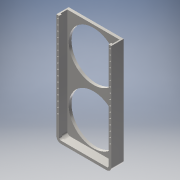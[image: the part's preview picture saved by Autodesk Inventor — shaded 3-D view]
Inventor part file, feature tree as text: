
AUTODESK INVENTOR PART (.ipt)
format: ipt  version: 2016 (Build 200138000, 138)  size: 247,296 bytes
history: native  units: mm
features: sketch x6, projected_geometry x6, extrude x4, hole x2
ambient origin geometry x8: Origin, YZ Plane, XZ Plane, XY Plane, X Axis, Y Axis, Z Axis, Center Point
bodies: Solid1 (feature_tree)
feature tree (18):
  extrude  "Extrusion1"  Depth=240.0mm
  extrude  "Extrusion2"  Depth=6.0mm
  extrude  "Extrusion3"  Depth=6.0mm
  extrude  "Extrusion4"  Depth=3.0mm
  hole  "Hole1"  [1 undecoded]
  hole  "Hole2"  [1 undecoded]
  sketch  "Sketch1"  dims[d0=120.0mm d1=240.0mm]
  sketch  "Sketch2"  dims[d2=120.0mm d3=6.0mm]
  projected_geometry  "Projected Loop1"
  sketch  "Sketch3"  dims[d4=10.0mm d5=6.0mm]
  projected_geometry  "Projected Loop2"
  sketch  "Sketch5"  dims[d6=0.0mm d7=3.0mm]
  projected_geometry  "Projected Loop3"
  sketch  "Sketch6"  dims[d8=15.0mm d9=0.0mm]
  projected_geometry  "Projected Loop4"
  sketch  "Sketch7"  dims[d10=3.0mm d11=6.0mm d12=0.0mm d13=6.0mm d14=0.0mm d15=18.0mm d16=9.0mm d17=3.1mm d18=6.0mm d19=4.0mm d20=2.0mm d21=90.0deg d22=4.0mm d23=20.594885mm d24=6.0mm d25=160.0mm d27=12.0mm d28=10.0mm d30=10.0mm d32=3.1mm d33=6.0mm d34=4.0mm d35=2.0mm d36=90.0deg d37=4.0mm d38=20.594885mm]
  projected_geometry  "Projected Loop5"
  projected_geometry  "Projected Loop6"
note: 2 required parameter values undecoded (feature->parameter linkage not recoverable at this tier; creation-order binding heuristic only, values carry confidence <= 0.55)
